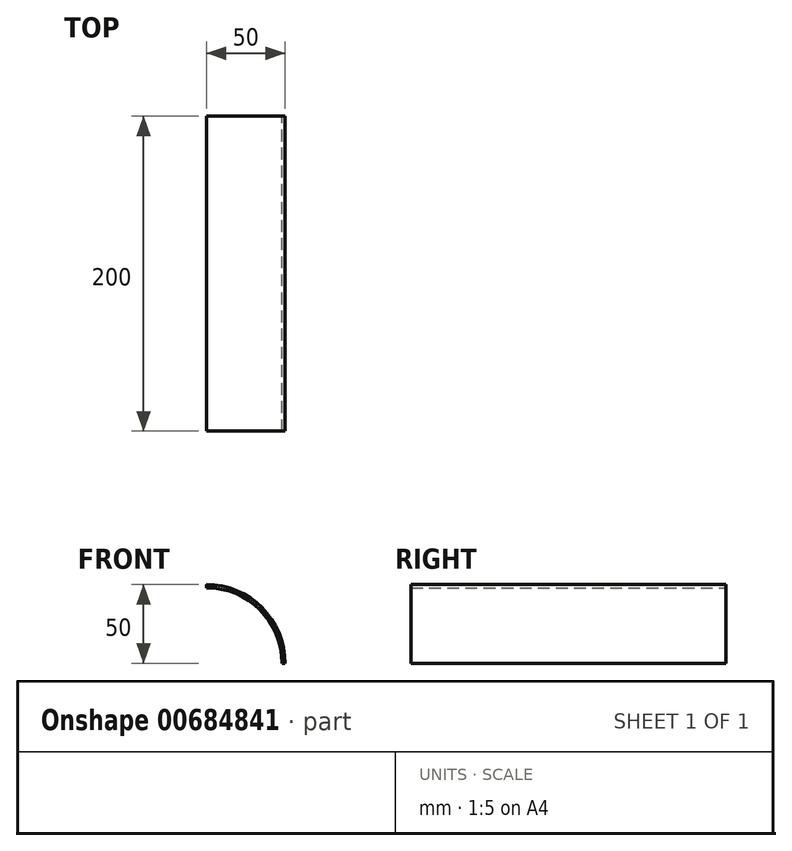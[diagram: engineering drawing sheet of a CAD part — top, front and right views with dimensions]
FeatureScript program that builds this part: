
annotation { "Feature Type Name" : "Feature", "Feature Type Description" : "" }
export const myFeature = defineFeature(function(context is Context, id is Id, definition is map)
    precondition{}
    {
        {
            var Q0;
            Q0=qCreatedBy(makeId("Front.planeOp"),FACE);
            var sketch = newSketch(context, id + "F0", { "sketchPlane" : qUnion([Q0])});
            skLineSegment(sketch, "E0", {"start": v(0, 48) * mm, "end": v(0, 50) * mm});
            skLineSegment(sketch, "E1", {"start": v(48, 0) * mm, "end": v(50, 0) * mm});
            skArc(sketch, "E2", {"start": v(50, 0) * mm, "mid": v(35.36, 35.36) * mm, "end": v(0, 50) * mm});
            skArc(sketch, "E3", {"start": v(48, 0) * mm, "mid": v(33.94, 33.94) * mm, "end": v(0, 48) * mm});
            skSolve(sketch);
        }
        {
            var Q0;
            Q0=makeQuery(id+"F0.imprint","IMPRINT",FACE,{"disambiguationData":[TD([[makeQuery(id+"F0.imprint","IMPRINT",EDGE,{"derivedFrom":sQuery(id+"F0.wireOp",EDGE,"E2")}),1.0]])]});
            extrude(context, id + "F1", {"entities" : qUnion([Q0]), "depth" : 200 * mm, "offsetDistance" : 25 * mm});
        }
    });
